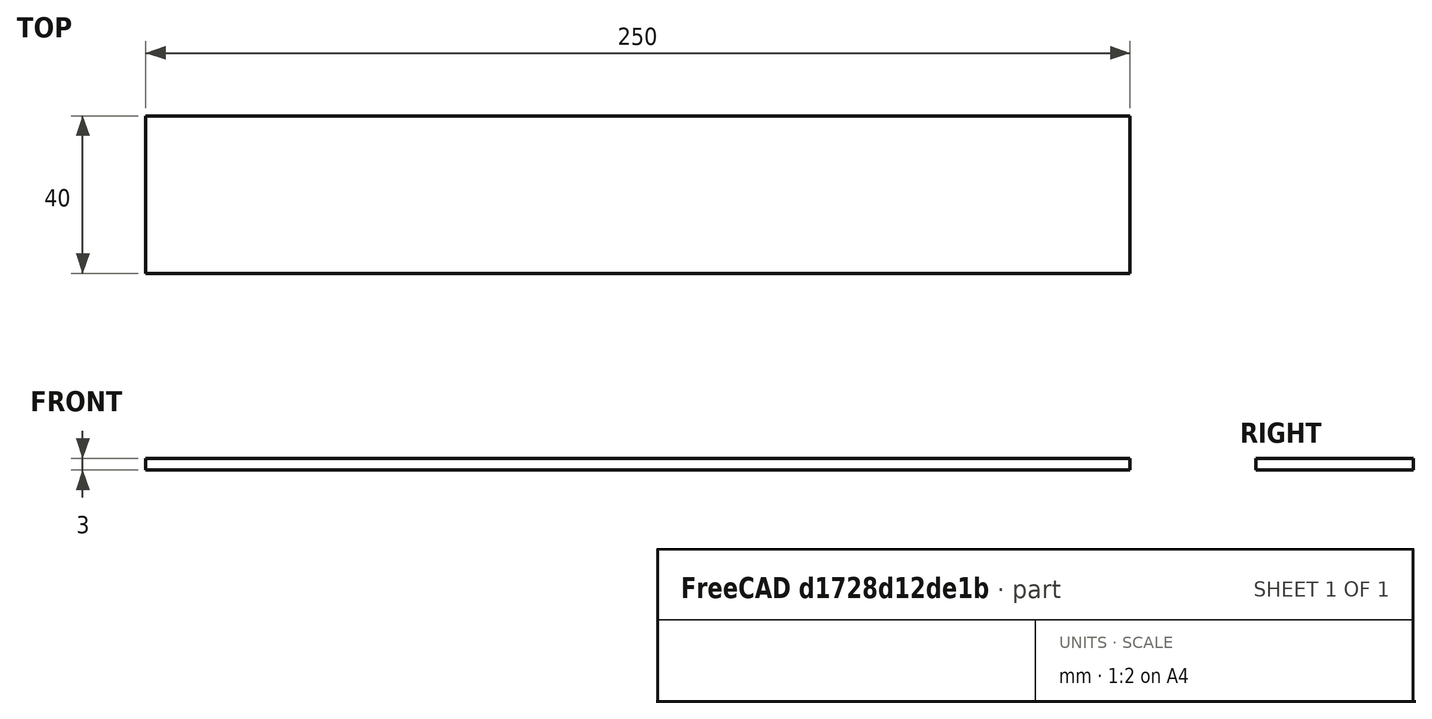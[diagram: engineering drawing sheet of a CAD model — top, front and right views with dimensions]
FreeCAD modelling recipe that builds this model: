
FCSTD DOCUMENT  (FreeCAD 0.17R13528 (Git))
Label: listones
License: All rights reserved
LicenseURL: http://en.wikipedia.org/wiki/All_rights_reserved
objects: Sketcher::SketchObject×1, PartDesign::Pad×1, Part::Part2DObjectPython×1
note: 4 computed .brp shape members not serialized (recipe doc carries the construction recipe); baked Part::Feature solids carry a one-line shape summary decoded from their .brp

FEATURE [Sketcher::SketchObject] Sketch
  MapMode = 5
  sketch-geometry (4):
    g0: LineSegment StartX=-125 StartY=20 StartZ=0 EndX=125 EndY=20 EndZ=0
    g1: LineSegment StartX=125 StartY=20 StartZ=0 EndX=125 EndY=-20 EndZ=0
    g2: LineSegment StartX=125 StartY=-20 StartZ=0 EndX=-125 EndY=-20 EndZ=0
    g3: LineSegment StartX=-125 StartY=-20 StartZ=0 EndX=-125 EndY=20 EndZ=0
  constraints (13):
    c: Coincident(g0,g1)
    c: Coincident(g1,g2)
    c: Coincident(g2,g3)
    c: Coincident(g3,g0)
    c: Horizontal(g0)
    c: Vertical(g1)
    c: Vertical(g3)
    c: DistanceY(g3,g3) = 40
    c: Equal(g1,g3)
    c: Equal(g0,g2)
    c: DistanceX(g0,g0) = 250
    c: Symmetric(g2,g1,g-2)
    c: Symmetric(g1,g0,g-1)
FEATURE [PartDesign::Pad] Pad
  Length = 3
  Length2 = 100
  Profile = -> Sketch
  Type = 0
FEATURE [Part::Part2DObjectPython] Shape2DView  # Draft 2D object (typed FeaturePython)
  Base = -> Pad
  HiddenLines = false
  InPlace = true
  Projection = (0,0,1)
  ProjectionMode = 0
  SegmentLength = 0.05
  Tessellation = false
  VisibleOnly = false
